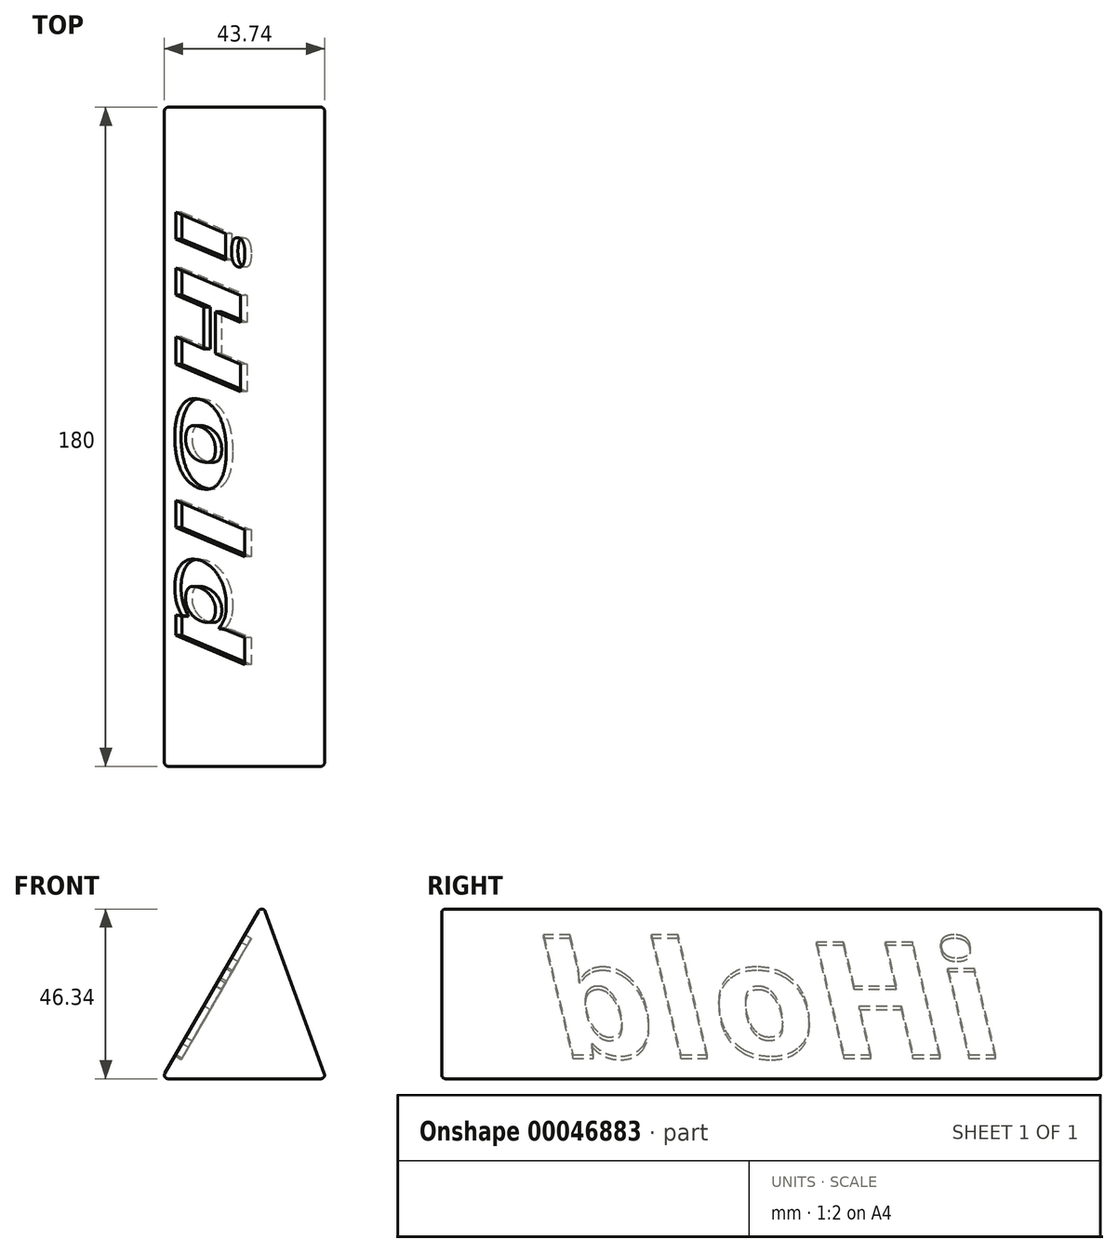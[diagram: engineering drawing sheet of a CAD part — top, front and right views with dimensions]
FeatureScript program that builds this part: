
annotation { "Feature Type Name" : "Feature", "Feature Type Description" : "" }
export const myFeature = defineFeature(function(context is Context, id is Id, definition is map)
    precondition{}
    {
        {
            var Q0;
            Q0=qCreatedBy(makeId("Front.planeOp"),FACE);
            var sketch = newSketch(context, id + "F0", { "sketchPlane" : qUnion([Q0])});
            skLineSegment(sketch, "E0", {"start": v(-27.54, 0) * mm, "end": v(17.36, 0) * mm});
            skLineSegment(sketch, "E1", {"start": v(17.36, 0) * mm, "end": v(0, 47.7) * mm});
            skLineSegment(sketch, "E2", {"start": v(0, 47.7) * mm, "end": v(-27.54, 0) * mm});
            skSolve(sketch);
        }
        {
            var Q0;
            Q0=makeQuery(id+"F0.imprint","IMPRINT",FACE,{"disambiguationData":[TD([[makeQuery(id+"F0.imprint","IMPRINT",EDGE,{"derivedFrom":sQuery(id+"F0.wireOp",EDGE,"E0")}),1.0]])]});
            extrude(context, id + "F1", {"entities" : qUnion([Q0]), "depth" : 180 * mm});
        }
        {
            var Q0;
            Q0=makeQuery(id+"F1.opExtrude","SWEPT_EDGE",EDGE,{"disambiguationData":[OSD([sQuery(id+"F0.wireOp",EDGE,"E1"),sQuery(id+"F0.wireOp",EDGE,"E2")])]});
            var Q1;
            Q1=makeQuery(id+"F1.opExtrude","CAP_FACE",FACE,{"disambiguationData":[OSD([sQuery(id+"F0.wireOp",EDGE,"E0"),sQuery(id+"F0.wireOp",EDGE,"E1"),sQuery(id+"F0.wireOp",EDGE,"E2")])],"isStart":false});
            var Q2;
            Q2=makeQuery(id+"F1.opExtrude","SWEPT_EDGE",EDGE,{"disambiguationData":[OSD([sQuery(id+"F0.wireOp",EDGE,"E0"),sQuery(id+"F0.wireOp",EDGE,"E1")])]});
            var Q3;
            Q3=makeQuery(id+"F1.opExtrude","SWEPT_EDGE",EDGE,{"disambiguationData":[OSD([sQuery(id+"F0.wireOp",EDGE,"E0"),sQuery(id+"F0.wireOp",EDGE,"E2")])]});
            var Q4;
            Q4=makeQuery(id+"F1.opExtrude","CAP_FACE",FACE,{"disambiguationData":[OSD([sQuery(id+"F0.wireOp",EDGE,"E0"),sQuery(id+"F0.wireOp",EDGE,"E1"),sQuery(id+"F0.wireOp",EDGE,"E2")])],"isStart":true});
            fillet(context, id + "F2", {"entities" : qUnion([Q0, Q1, Q2, Q3, Q4]), "radius" : 1 * mm, "tangentPropagation" : true, "allowEdgeOverflow" : false});
        }
        {
            var Q0;
            Q0=makeQuery(id+"F1.opExtrude","SWEPT_FACE",FACE,{"disambiguationData":[OSD([sQuery(id+"F0.wireOp",EDGE,"E2")])]});
            var sketch = newSketch(context, id + "F3", { "sketchPlane" : qUnion([Q0])});
            skText(sketch, "E3", { "text": "iHold", "fontName": "OpenSans-BoldItalic.ttf"});
            const initialGuessF3  = {"E3": [0.02779, -0.00617, 1, 0, 0.03582]};
            skSetInitialGuess(sketch, initialGuessF3);
            skSolve(sketch);
        }
        {
            var Q0;
            Q0=makeQuery(id+"F3.imprint","IMPRINT",FACE,{"disambiguationData":[TD([[makeQuery(id+"F3.imprint","IMPRINT",EDGE,{"derivedFrom":sQuery(id+"F3.wireOp",EDGE,"E3.sketch_text.stroke-7")}),-1.0]])]});
            var Q1;
            Q1=makeQuery(id+"F3.imprint","IMPRINT",FACE,{"disambiguationData":[TD([[makeQuery(id+"F3.imprint","IMPRINT",EDGE,{"derivedFrom":sQuery(id+"F3.wireOp",EDGE,"E3.sketch_text.stroke-0")}),-1.0]])]});
            var Q2;
            Q2=makeQuery(id+"F3.imprint","IMPRINT",FACE,{"disambiguationData":[TD([[makeQuery(id+"F3.imprint","IMPRINT",EDGE,{"derivedFrom":sQuery(id+"F3.wireOp",EDGE,"E3.sketch_text.stroke-11")}),-1.0]])]});
            var Q3;
            Q3=makeQuery(id+"F3.imprint","IMPRINT",FACE,{"disambiguationData":[TD([[makeQuery(id+"F3.imprint","IMPRINT",EDGE,{"derivedFrom":sQuery(id+"F3.wireOp",EDGE,"E3.sketch_text.stroke-23")}),-1.0]])]});
            var Q4;
            Q4=makeQuery(id+"F3.imprint","IMPRINT",FACE,{"disambiguationData":[TD([[makeQuery(id+"F3.imprint","IMPRINT",EDGE,{"derivedFrom":sQuery(id+"F3.wireOp",EDGE,"E3.sketch_text.stroke-41")}),-1.0]])]});
            var Q5;
            Q5=makeQuery(id+"F3.imprint","IMPRINT",FACE,{"disambiguationData":[TD([[makeQuery(id+"F3.imprint","IMPRINT",EDGE,{"derivedFrom":sQuery(id+"F3.wireOp",EDGE,"E3.sketch_text.stroke-45")}),-1.0]])]});
            extrude(context, id + "F4", {"entities" : qUnion([Q0, Q1, Q2, Q3, Q4, Q5]), "operationType" : NewBodyOperationType.REMOVE, "oppositeDirection" : true, "depth" : 2 * mm});
        }
    });
